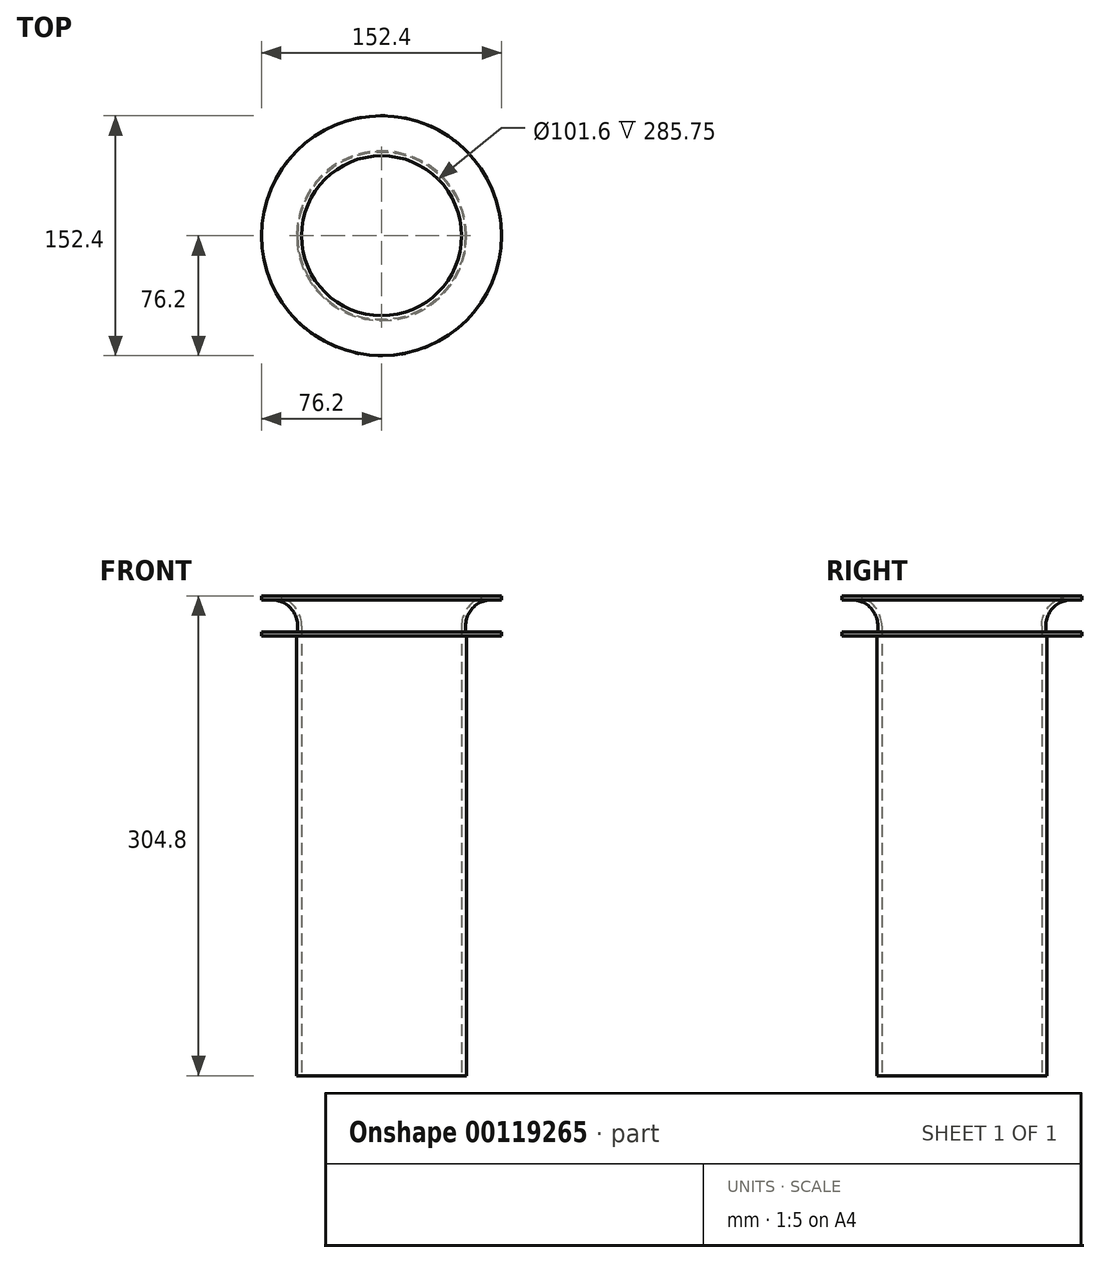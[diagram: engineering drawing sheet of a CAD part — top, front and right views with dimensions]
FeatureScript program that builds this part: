
annotation { "Feature Type Name" : "Feature", "Feature Type Description" : "" }
export const myFeature = defineFeature(function(context is Context, id is Id, definition is map)
    precondition{}
    {
        {
            var Q0;
            Q0=qCreatedBy(makeId("Top.planeOp"),FACE);
            var sketch = newSketch(context, id + "F0", { "sketchPlane" : qUnion([Q0])});
            skCircle(sketch, "E0", {"center": v(0, 0) * mm, "radius": 50.8 * mm});
            skCircle(sketch, "E1", {"center": v(0, 0) * mm, "radius": 76.2 * mm});
            skCircle(sketch, "E2", {"center": v(0, 0) * mm, "radius": 53.98 * mm});
            skSolve(sketch);
        }
        {
            var Q0;
            Q0=makeQuery(id+"F0.imprint","IMPRINT",FACE,{"disambiguationData":[TD([[makeQuery(id+"F0.imprint","IMPRINT",EDGE,{"derivedFrom":sQuery(id+"F0.wireOp",EDGE,"E0")}),-1.0]])]});
            var Q1;
            Q1=makeQuery(id+"F0.imprint","IMPRINT",FACE,{"disambiguationData":[TD([[makeQuery(id+"F0.imprint","IMPRINT",EDGE,{"derivedFrom":sQuery(id+"F0.wireOp",EDGE,"E1")}),1.0]])]});
            extrude(context, id + "F1", {"entities" : qUnion([Q0, Q1]), "depth" : 152.4 * mm});
        }
        {
            var Q0;
            Q0=makeQuery(id+"F1.opExtrude","CAP_EDGE",EDGE,{"disambiguationData":[OSD([sQuery(id+"F0.wireOp",EDGE,"E0")])],"isStart":false});
            fillet(context, id + "F2", {"entities" : qUnion([Q0]), "radius" : 19.05 * mm, "tangentPropagation" : true, "allowEdgeOverflow" : false});
        }
        {
            var Q0;
            Q0=makeQuery(id+"F0.imprint","IMPRINT",FACE,{"disambiguationData":[TD([[makeQuery(id+"F0.imprint","IMPRINT",EDGE,{"derivedFrom":sQuery(id+"F0.wireOp",EDGE,"E1")}),1.0]])]});
            extrude(context, id + "F3", {"entities" : qUnion([Q0]), "operationType" : NewBodyOperationType.REMOVE, "depth" : 127 * mm});
        }
        {
            var Q0;
            Q0=makeQuery(id+"F1.opExtrude","SWEPT_FACE",FACE,{"disambiguationData":[OSD([sQuery(id+"F0.wireOp",EDGE,"E1")])]});
            shell(context, id + "F4", {"entities" : qUnion([Q0]), "thickness" : 2.54 * mm});
        }
        {
            var Q0;
            Q0=makeQuery(id+"F4.opShell","OFFSET_FACE",FACE,{"disambiguationData":[OSD([sQuery(id+"F0.wireOp",EDGE,"E1"),sQuery(id+"F0.wireOp",EDGE,"E2")])]});
            extrude(context, id + "F5", {"entities" : qUnion([Q0]), "operationType" : NewBodyOperationType.REMOVE, "oppositeDirection" : true, "depth" : 1 / 203.2 * mm});
        }
        {
            var Q0;
            Q0=makeQuery(id+"F0.imprint","IMPRINT",FACE,{"disambiguationData":[TD([[makeQuery(id+"F0.imprint","IMPRINT",EDGE,{"derivedFrom":sQuery(id+"F0.wireOp",EDGE,"E0")}),-1.0]])]});
            extrude(context, id + "F6", {"entities" : qUnion([Q0]), "operationType" : NewBodyOperationType.ADD, "oppositeDirection" : true, "depth" : 152.4 * mm});
        }
    });
